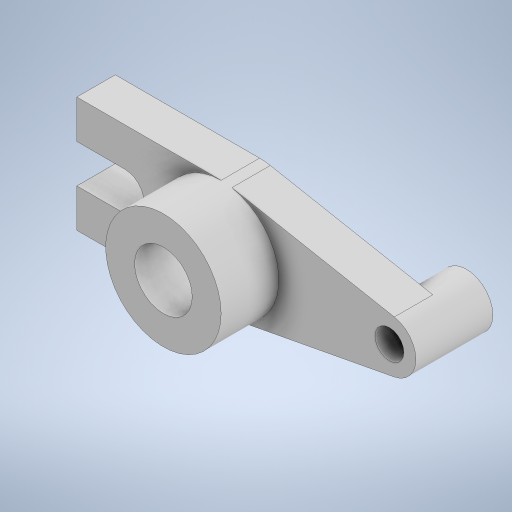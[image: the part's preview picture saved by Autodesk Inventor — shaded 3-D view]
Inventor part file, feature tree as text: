
AUTODESK INVENTOR PART (.ipt)
format: ipt  version: 2023 (Build 270158000, 158)  size: 270,848 bytes
history: native  units: mm
features: extrude x3, sketch x1
ambient origin geometry x8: Origin, YZ Plane, XZ Plane, XY Plane, X Axis, Y Axis, Z Axis, Center Point
bodies: Solido1 (feature_tree)
feature tree (4):
  sketch  "Schizzo1"
  extrude  "Estrusione1"  Depth=10.0mm
  extrude  "Estrusione2"  Depth=12.0mm
  extrude  "Estrusione3"  Depth=24.0mm
